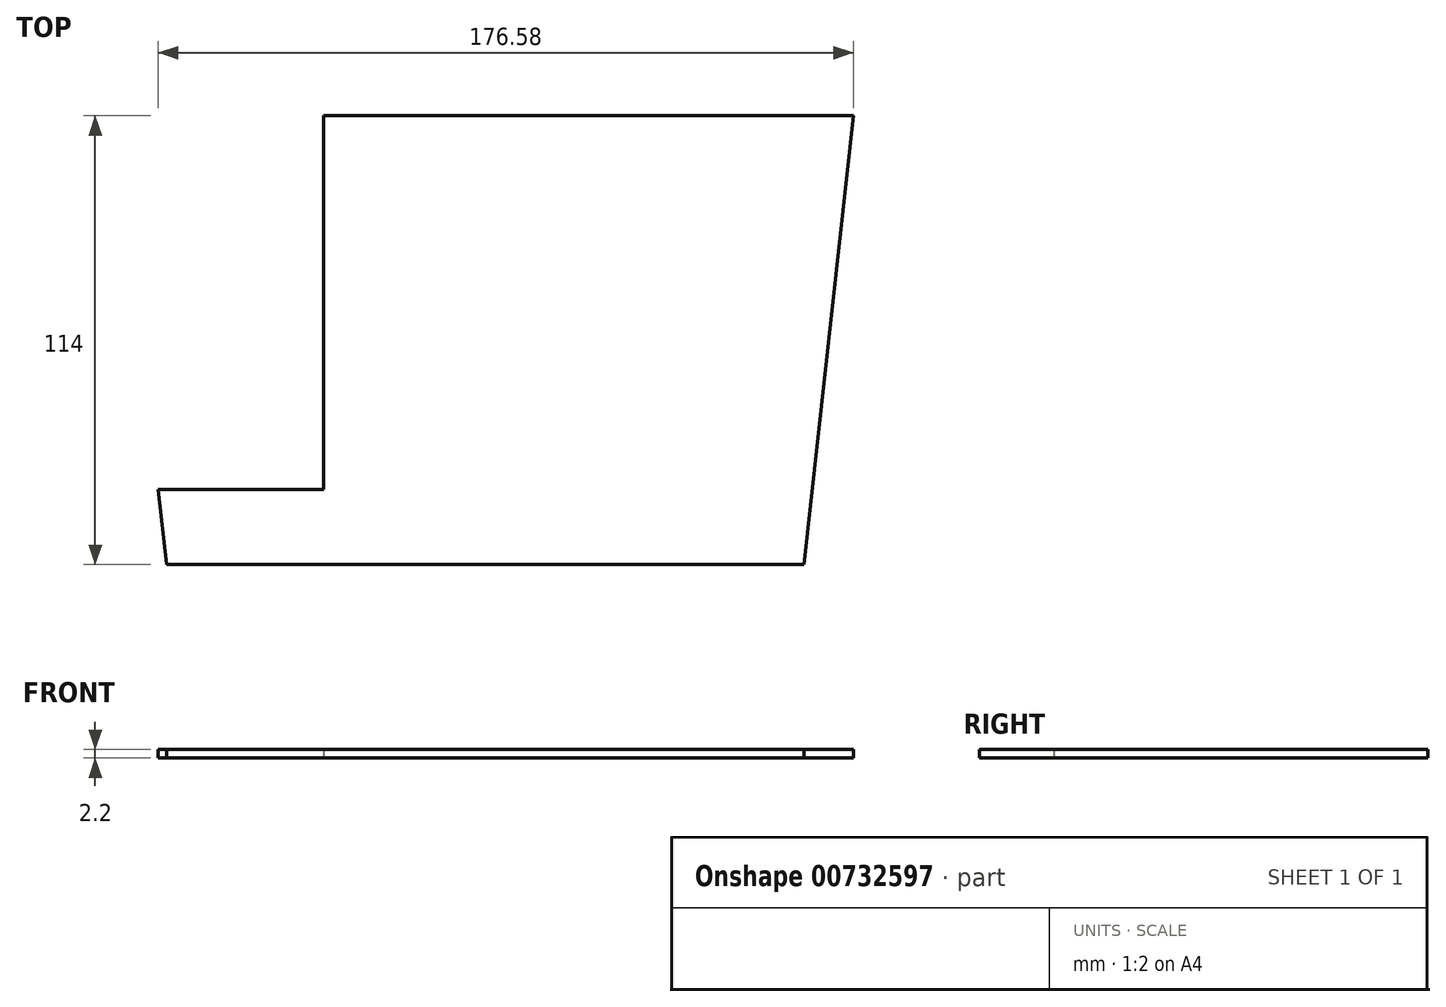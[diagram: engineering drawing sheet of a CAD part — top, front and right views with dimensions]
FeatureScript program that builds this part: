
annotation { "Feature Type Name" : "Feature", "Feature Type Description" : "" }
export const myFeature = defineFeature(function(context is Context, id is Id, definition is map)
    precondition{}
    {
        {
            var Q0;
            Q0=qCreatedBy(makeId("Top.planeOp"),FACE);
            var sketch = newSketch(context, id + "F0", { "sketchPlane" : qUnion([Q0])});
            skLineSegment(sketch, "E0", {"start": v(-81, 0) * mm, "end": v(81, 0) * mm});
            skPoint(sketch, "E1", {"position": v(0, 0) * mm});
            skLineSegment(sketch, "E2", {"start": v(-41.08, 114) * mm, "end": v(93.5, 114) * mm});
            skPoint(sketch, "E3", {"position": v(0, 114) * mm});
            skLineSegment(sketch, "E4", {"start": v(-83.08, 19) * mm, "end": v(-81, 0) * mm});
            skLineSegment(sketch, "E5", {"start": v(93.5, 114) * mm, "end": v(81, 0) * mm});
            skLineSegment(sketch, "E6", {"start": v(-83.08, 19) * mm, "end": v(-41.08, 19) * mm});
            skLineSegment(sketch, "E7", {"start": v(-41.08, 114) * mm, "end": v(-41.08, 19) * mm});
            skPoint(sketch, "E8.orphan", {"position": v(-93.5, 114) * mm});
            skSolve(sketch);
        }
        {
            var Q0;
            Q0=makeQuery(id+"F0.imprint","IMPRINT",FACE,{"disambiguationData":[TD([[makeQuery(id+"F0.imprint","IMPRINT",EDGE,{"derivedFrom":sQuery(id+"F0.wireOp",EDGE,"E0")}),1.0]])]});
            extrude(context, id + "F1", {"entities" : qUnion([Q0]), "depth" : 2.2 * mm, "offsetDistance" : 25 * mm});
        }
    });
